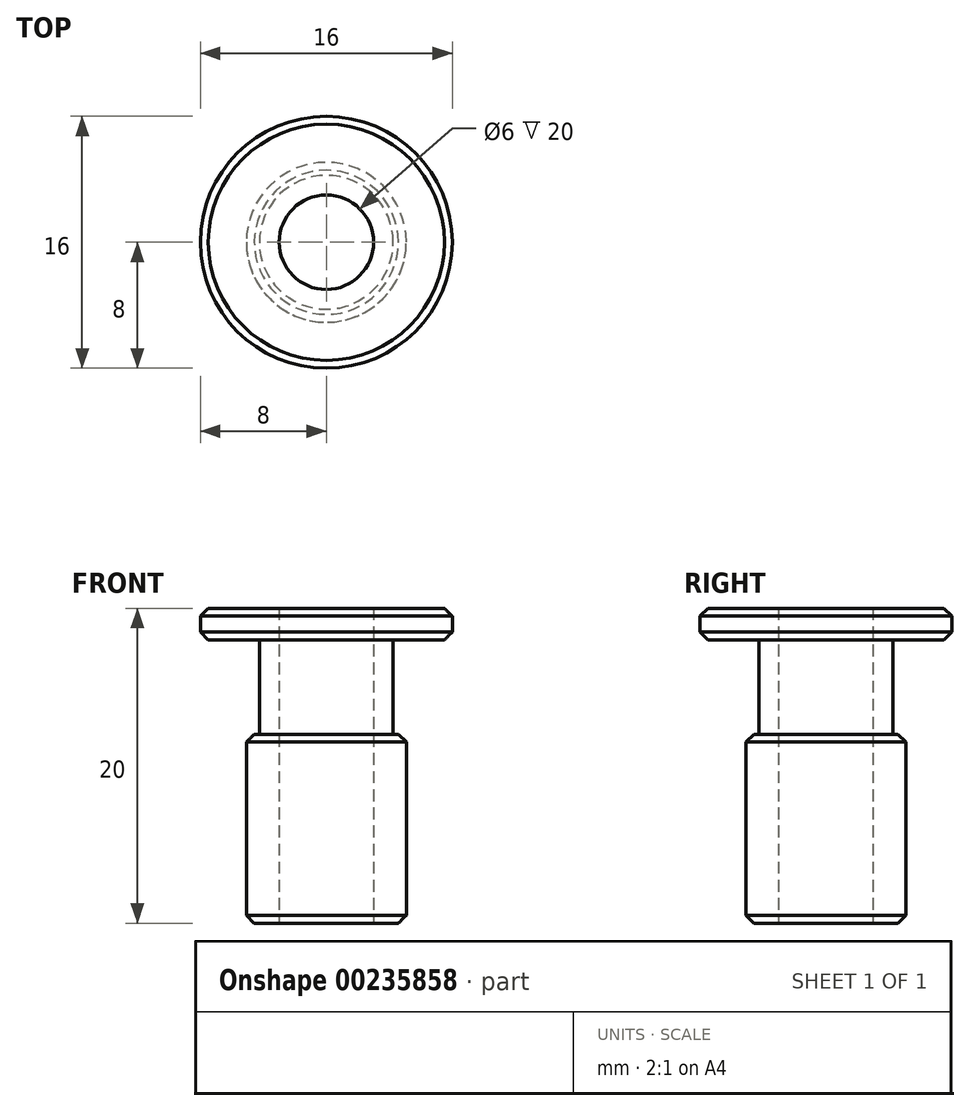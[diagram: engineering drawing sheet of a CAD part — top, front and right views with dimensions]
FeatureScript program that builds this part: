
annotation { "Feature Type Name" : "Feature", "Feature Type Description" : "" }
export const myFeature = defineFeature(function(context is Context, id is Id, definition is map)
    precondition{}
    {
        {
            var Q0;
            Q0=qCreatedBy(makeId("Top.planeOp"),FACE);
            var sketch = newSketch(context, id + "F0", { "sketchPlane" : qUnion([Q0])});
            skCircle(sketch, "E0", {"center": v(0, 0) * mm, "radius": 8 * mm});
            skCircle(sketch, "E1", {"center": v(0, 0) * mm, "radius": 3 * mm});
            skSolve(sketch);
        }
        {
            var Q0;
            Q0=qCreatedBy(makeId("Front.planeOp"),FACE);
            var sketch = newSketch(context, id + "F1", { "sketchPlane" : qUnion([Q0])});
            skLineSegment(sketch, "E2.0", {"start": v(3, 0) * mm, "end": v(3, -18) * mm});
            skLineSegment(sketch, "E3.0", {"start": v(-3, 0) * mm, "end": v(-3, -18) * mm});
            skLineSegment(sketch, "E4.0", {"start": v(-4.25, 0) * mm, "end": v(-4.25, -18) * mm});
            skLineSegment(sketch, "E5.0", {"start": v(4.25, 0) * mm, "end": v(4.25, -18) * mm});
            skLineSegment(sketch, "E6.0", {"start": v(-5.08, -6) * mm, "end": v(-5.08, -18) * mm});
            skLineSegment(sketch, "E7.0", {"start": v(5.12, -6) * mm, "end": v(5.12, -18) * mm});
            skLineSegment(sketch, "E8", {"start": v(-3, -18) * mm, "end": v(-5.08, -18) * mm});
            skLineSegment(sketch, "E9", {"start": v(3, -18) * mm, "end": v(5.12, -18) * mm});
            skLineSegment(sketch, "E10", {"start": v(-5.08, -6) * mm, "end": v(-4.25, -6) * mm});
            skLineSegment(sketch, "E11", {"start": v(5.12, -6) * mm, "end": v(4.25, -6) * mm});
            skLineSegment(sketch, "E12", {"start": v(-4.25, 0) * mm, "end": v(-3, 0) * mm});
            skLineSegment(sketch, "E13", {"start": v(3, 0) * mm, "end": v(4.25, 0) * mm});
            skLineSegment(sketch, "E14", {"start": v(0, 0) * mm, "end": v(0, -18) * mm, "construction": true});
            skSolve(sketch);
        }
        {
            var Q0;
            Q0 = qSketchRegion(id + "F0", true);
            extrude(context, id + "F2", {"entities" : qUnion([Q0]), "depth" : 2 * mm});
        }
        {
            var Q0;
            Q0=makeQuery(id+"F2.opExtrude","SWEPT_FACE",FACE,{"disambiguationData":[OSD([sQuery(id+"F0.wireOp",EDGE,"E0")])]});
            chamfer(context, id + "F3", {"entities" : qUnion([Q0]), "chamferType" : ChamferType.OFFSET_ANGLE, "width" : .5 * mm, "oppositeDirection" : false, "angle" : 45 * degree, "tangentPropagation" : true});
        }
        {
            var Q0;
            {var subQ1=sQuery(id+"F1.wireOp",EDGE,"E3.0");Q0=makeQuery(id+"F1.imprint","IMPRINT",FACE,{"disambiguationData":[TD([[makeQuery(id+"F1.imprint","IMPRINT",EDGE,{"derivedFrom":subQ1}),-1.0]])]});}
            var Q1;
            {var subQ4=sQuery(id+"F1.wireOp",EDGE,"E6.0");Q1=makeQuery(id+"F1.imprint","IMPRINT",FACE,{"disambiguationData":[TD([[makeQuery(id+"F1.imprint","IMPRINT",EDGE,{"derivedFrom":subQ4}),1.0]])]});}
            var Q2;
            Q2=sQuery(id+"F1.wireOp",EDGE,"E14");
            revolve(context, id + "F4", {"operationType" : NewBodyOperationType.ADD, "entities" : qUnion([Q0, Q1]), "axis" : qUnion([Q2]), "revolveType" : RevolveType.FULL});
        }
        {
            var Q0;
            Q0=makeQuery(id+"F4.opRevolve","SWEPT_EDGE",EDGE,{"disambiguationData":[OSD([sQuery(id+"F1.wireOp",EDGE,"E6.0"),sQuery(id+"F1.wireOp",EDGE,"E10")])]});
            var Q1;
            Q1=makeQuery(id+"F4.opRevolve","SWEPT_EDGE",EDGE,{"disambiguationData":[OSD([sQuery(id+"F1.wireOp",EDGE,"E6.0"),sQuery(id+"F1.wireOp",EDGE,"E8")])]});
            chamfer(context, id + "F5", {"entities" : qUnion([Q0, Q1]), "chamferType" : ChamferType.OFFSET_ANGLE, "width" : .5 * mm, "oppositeDirection" : false, "angle" : 45 * degree, "tangentPropagation" : true});
        }
    });
